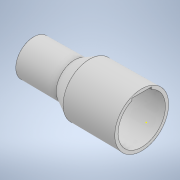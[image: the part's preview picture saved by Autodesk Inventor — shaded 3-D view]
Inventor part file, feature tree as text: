
AUTODESK INVENTOR PART (.ipt)
format: ipt  version: 2020 (Build 240168000, 168)  size: 172,032 bytes
history: native  units: mm
features: sketch x3, plane x2, revolve x1, extrude x1, projected_geometry x1
ambient origin geometry x8: Origin, YZ Plane, XZ Plane, XY Plane, X Axis, Y Axis, Z Axis, Center Point
bodies: Solid1 (feature_tree)
feature tree (8):
  revolve  "Revolution1"  [1 undecoded]
  plane  "Work Plane1"
  extrude  "Extrusion1"  Depth=0.156237mm
  sketch  "Sketch3"  dims[d8=2.0mm d9=0.2mm d10=0.2mm d11=9.0mm d12=0.0mm d16=0.0mm d17=25.0mm d18=11.25mm d19=11.0mm d20=0.0mm d21=2.0mm d22=90.0deg d23=25.0mm d24=35.0mm d25=12.0mm d26=6.0mm d27=6.788mm d28=0.0mm d29=-2.806mm d31=0.5mm d32=0.872665mm d33=0.5mm d34=0.872665mm d35=0.872665mm d36=0.5mm d37=0.872665mm]
  plane  "Work Plane2"
  sketch  "Sketch1"  dims[d1=14.5mm d2=14.0mm]
  sketch  "Sketch2"  dims[d5=32.0mm d6=0.156237mm d7=3.0mm]
  projected_geometry  "Projected Loop1"
note: 1 required parameter value undecoded (feature->parameter linkage not recoverable at this tier; creation-order binding heuristic only, values carry confidence <= 0.55)
